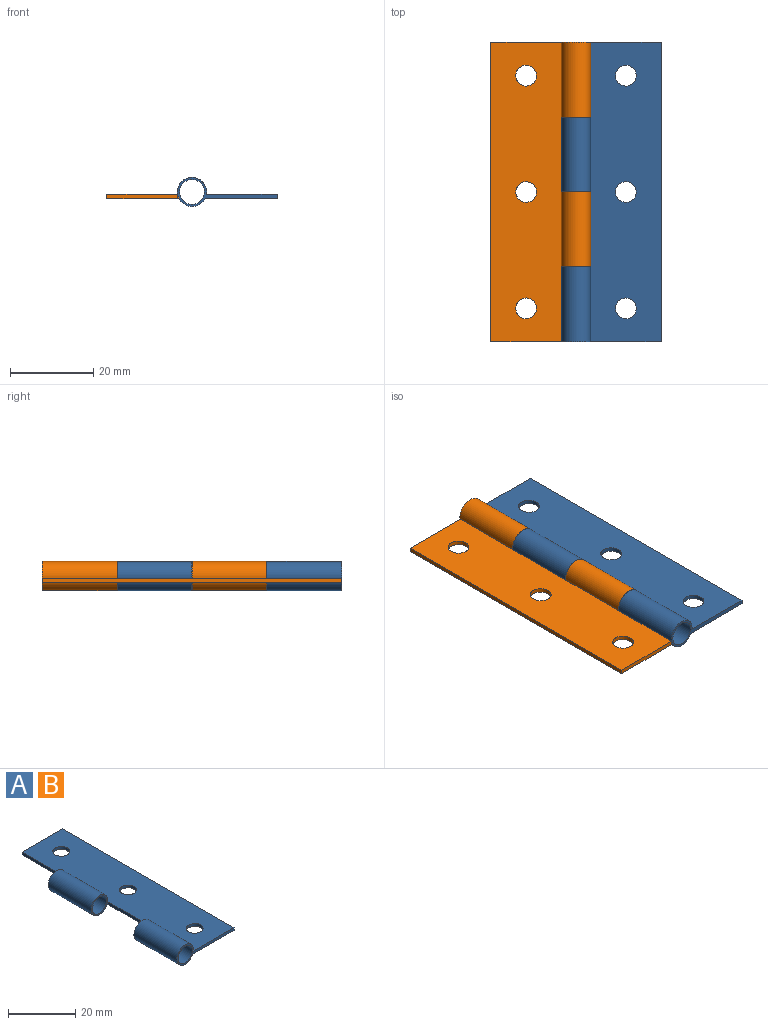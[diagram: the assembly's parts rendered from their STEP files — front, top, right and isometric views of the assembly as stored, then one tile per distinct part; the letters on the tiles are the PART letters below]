
ASSEMBLY  parts=2 mates=1
PART A: 17 faces, bbox 24x72x7 mm
  f0: plane 18x1mm, normal (-1,0,0), area 18mm2, adj f8,f9,f12,f16
  f1: plane 24x7mm, normal (0,-1,0), area 27.4mm2, adj f2,f8,f9,f14,f15
  f2: plane 72x1mm, normal (1,0,0), area 72mm2, adj f1,f3,f8,f9
  f3: plane 17x1mm, normal (0,1,0), area 17mm2, adj f2,f7,f8,f9
  f4: cylinder r=2.5mm len=5mm, axis (0,0,-1), area 15.7mm2, adj f8,f9
  f5: cylinder r=2.5mm len=5mm, axis (0,0,-1), area 15.7mm2, adj f8,f9
  f6: cylinder r=2.5mm len=5mm, axis (0,0,-1), area 15.7mm2, adj f8,f9
  f7: plane 18x1mm, normal (-1,0,0), area 18mm2, adj f3,f8,f9,f13
  f8: plane 72x17.04mm, normal (0,0,1), area 1166.4mm2, adj f0,f1,f2,f3,f4,f5,f6,f7
  f9: plane 72x17.34mm, normal (0,0,-1), area 1177.3mm2, adj f0,f1,f2,f3,f4,f5,f6,f7
  f10: cylinder r=3.5mm len=18mm, axis (0,1,0), area 377mm2, adj f8,f9,f12,f13
  f11: cylinder r=3mm len=18mm, axis (0,1,0), area 339.3mm2, adj f12,f13
  f12: plane 7x7mm, normal (0,-1,0), area 10.4mm2, adj f0,f8,f9,f10,f11
  f13: plane 7x7mm, normal (0,1,0), area 10.4mm2, adj f7,f8,f9,f10,f11
  f14: cylinder r=3.5mm len=18mm, axis (0,1,0), area 377mm2, adj f1,f8,f9,f16
  f15: cylinder r=3mm len=18mm, axis (0,1,0), area 339.3mm2, adj f1,f16
  f16: plane 7x7mm, normal (0,1,0), area 10.4mm2, adj f0,f8,f9,f14,f15
PART B: same geometry as A
PLACE A t=(5.33,-5,3.34)mm fixed
PLACE B rot(axis=(0,0,-1),180deg) t=(-18.66,-5,3.28)mm
MATE revolute B.f10 <-> A.f10  axis (0,-1,0) through (-6.67,31,4.84)mm
